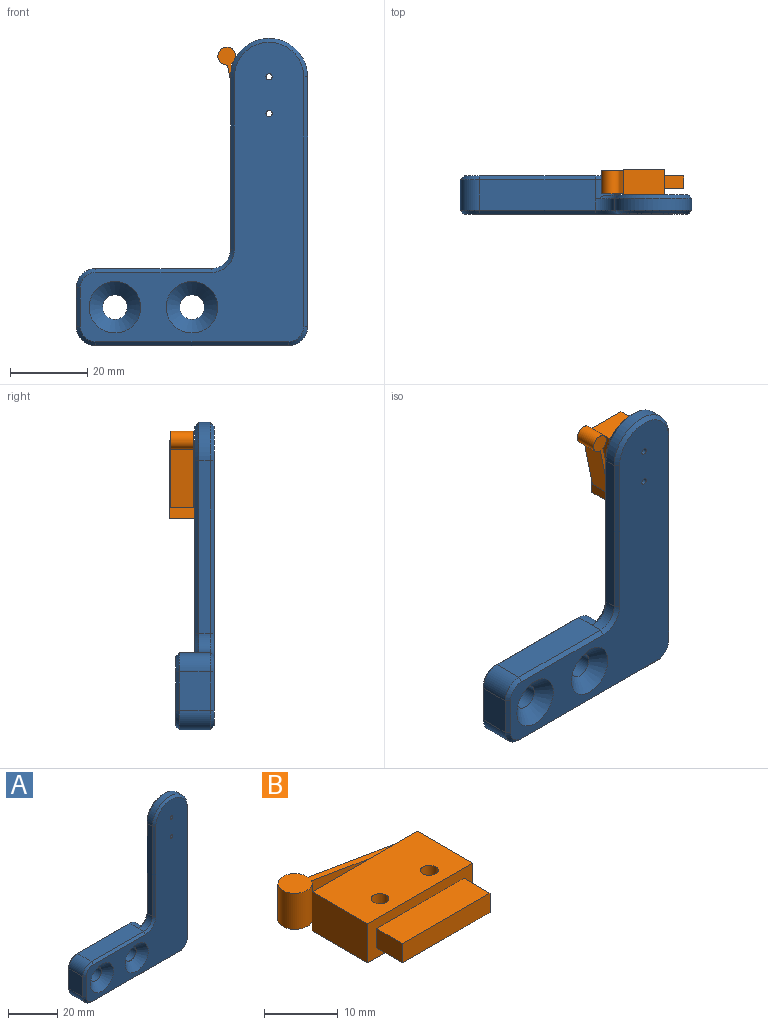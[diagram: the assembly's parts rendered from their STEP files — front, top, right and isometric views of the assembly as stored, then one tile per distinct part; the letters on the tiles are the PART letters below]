
ASSEMBLY  parts=2 mates=1
PART A: 48 faces, bbox 60x10x79.8 mm
  f0: plane 64.75x3mm, normal (1,0,0), area 194.2mm2, adj f3,f20,f26,f45
  f1: plane 38x18mm, normal (0,1,0), area 559.4mm2, adj f32,f33,f34,f35,f36,f37,f38,f39
  f2: plane 50x8mm, normal (0,0,-1), area 300mm2, adj f17,f19,f20,f30,f34,f47
  f3: cylinder r=10mm len=20mm, axis (0,1,0), area 94.2mm2, adj f0,f4,f24,f44
  f4: plane 44.75x3mm, normal (-1,0,0), area 134.2mm2, adj f3,f21,f22,f43
  f5: plane 30x8mm, normal (0,0,1), area 240mm2, adj f16,f18,f21,f25,f37
  f6: cylinder r=3.2mm len=6.4mm, axis (0,1,0), area 110.6mm2, adj f13,f41
  f7: cylinder r=0.8mm len=5mm, axis (0,1,0), area 25.1mm2, adj f11,f14
  f8: cylinder r=0.8mm len=5mm, axis (0,1,0), area 25.1mm2, adj f11,f14
  f9: plane 10x8mm, normal (-1,0,0), area 80mm2, adj f18,f19,f29,f33
  f10: cylinder r=3.2mm len=6.4mm, axis (0,1,0), area 110.6mm2, adj f12,f40
  f11: plane 77.75x58mm, normal (0,-1,0), area 1796.1mm2, adj f7,f8,f12,f13,f22,f23,f24,f25
  f12: cone r=3.2mm half-angle=45deg, axis (0,-1,0), area 153.9mm2, adj f10,f11
  f13: cone r=3.2mm half-angle=45deg, axis (0,-1,0), area 153.9mm2, adj f6,f11
  f14: plane 77.75x21.72mm, normal (0,1,0), area 1387.3mm2, adj f7,f8,f15,f16,f17,f42,f43,f44
  f15: plane 10x4mm, normal (1,0,0), area 40mm2, adj f14,f16,f17,f38
  f16: cylinder r=5mm len=5mm, axis (0,-1,0), area 33mm2, adj f5,f14,f15,f39,f42
  f17: cylinder r=5mm len=5mm, axis (0,-1,0), area 33.5mm2, adj f2,f14,f15,f36,f47
  f18: cylinder r=5mm len=8mm, axis (0,1,0), area 62.8mm2, adj f5,f9,f27,f35
  f19: cylinder r=5mm len=8mm, axis (0,1,0), area 62.8mm2, adj f2,f9,f31,f32
  f20: cylinder r=5mm len=5mm, axis (0,1,0), area 23.6mm2, adj f0,f2,f28,f46
  f21: cylinder r=5mm len=5mm, axis (0,-1,0), area 23.6mm2, adj f4,f5,f23,f42
  f22: plane 44.75x1mm, normal (-0.71,-0.71,0), area 63.3mm2, adj f4,f11,f23,f24
  f23: cone r=6mm half-angle=45deg, axis (0,-1,0), area 12.2mm2, adj f11,f21,f22,f25
  f24: cone r=9mm half-angle=45deg, axis (0,1,0), area 42.2mm2, adj f3,f11,f22,f26
  f25: plane 30x1mm, normal (0,-0.71,0.71), area 42.4mm2, adj f5,f11,f23,f27
  f26: plane 64.75x1mm, normal (0.71,-0.71,0), area 91.6mm2, adj f0,f11,f24,f28
  f27: cone r=4mm half-angle=45deg, axis (0,1,0), area 10mm2, adj f11,f18,f25,f29
  f28: cone r=4mm half-angle=45deg, axis (0,1,0), area 10mm2, adj f11,f20,f26,f30
  f29: plane 10x1mm, normal (-0.71,-0.71,0), area 14.1mm2, adj f9,f11,f27,f31
  f30: plane 50x1mm, normal (0,-0.71,-0.71), area 70.7mm2, adj f2,f11,f28,f31
  f31: cone r=4mm half-angle=45deg, axis (0,1,0), area 10mm2, adj f11,f19,f29,f30
  f32: cone r=4mm half-angle=45deg, axis (0,-1,0), area 10mm2, adj f1,f19,f33,f34
  f33: plane 10x1mm, normal (-0.71,0.71,0), area 14.1mm2, adj f1,f9,f32,f35
  f34: plane 30x1mm, normal (0,0.71,-0.71), area 42.4mm2, adj f1,f2,f32,f36
  f35: cone r=4mm half-angle=45deg, axis (0,-1,0), area 10mm2, adj f1,f18,f33,f37
  f36: cone r=4mm half-angle=45deg, axis (0,-1,0), area 10mm2, adj f1,f17,f34,f38
  f37: plane 30x1mm, normal (0,0.71,0.71), area 42.4mm2, adj f1,f5,f35,f39
  f38: plane 10x1mm, normal (0.71,0.71,0), area 14.1mm2, adj f1,f15,f36,f39
  f39: cone r=4mm half-angle=45deg, axis (0,-1,0), area 10mm2, adj f1,f16,f37,f38
  f40: cone r=4.2mm half-angle=45deg, axis (0,1,0), area 32.9mm2, adj f1,f10
  f41: cone r=4.2mm half-angle=45deg, axis (0,1,0), area 32.9mm2, adj f1,f6
  f42: cone r=6mm half-angle=45deg, axis (0,1,0), area 10mm2, adj f14,f16,f21,f43
  f43: plane 44.75x1mm, normal (-0.71,0.71,0), area 63.3mm2, adj f4,f14,f42,f44
  f44: cone r=10mm half-angle=45deg, axis (0,-1,0), area 42.2mm2, adj f3,f14,f43,f45
  f45: plane 64.75x1mm, normal (0.71,0.71,0), area 91.6mm2, adj f0,f14,f44,f46
  f46: cone r=4mm half-angle=45deg, axis (0,-1,0), area 10mm2, adj f14,f20,f45,f47
  f47: plane 20x1mm, normal (0,0.71,-0.71), area 25.4mm2, adj f2,f14,f17,f46
PART B: 18 faces, bbox 22.6x21.3x6.5 mm
  f0: plane 20.25x6.5mm, normal (0,-1,0), area 77.9mm2, adj f1,f5,f6,f7,f8,f9,f11,f12
  f1: plane 10.7x6.5mm, normal (1,0,0), area 69.5mm2, adj f0,f2,f6,f7
  f2: plane 20.25x6.5mm, normal (0,1,0), area 101.6mm2, adj f1,f5,f6,f7,f14,f15,f16,f17
  f3: cylinder r=1.2mm len=6.5mm, axis (0,0,-1), area 49mm2, adj f6,f7
  f4: cylinder r=1.2mm len=6.5mm, axis (0,0,-1), area 49mm2, adj f6,f7
  f5: plane 10.7x6.5mm, normal (-1,0,0), area 69.5mm2, adj f0,f2,f6,f7
  f6: plane 20.25x10.7mm, normal (0,0,1), area 207.6mm2, adj f0,f1,f2,f3,f4,f5
  f7: plane 20.25x10.7mm, normal (0,0,-1), area 207.6mm2, adj f0,f1,f2,f3,f4,f5
  f8: plane 5x3.2mm, normal (1,0,0), area 16mm2, adj f0,f10,f11,f12
  f9: plane 5x3.2mm, normal (-1,0,0), area 16mm2, adj f0,f10,f11,f12
  f10: plane 16.8x3.2mm, normal (0,-1,0), area 53.8mm2, adj f8,f9,f11,f12
  f11: plane 16.8x5mm, normal (0,0,1), area 84mm2, adj f0,f8,f9,f10
  f12: plane 16.8x5mm, normal (0,0,-1), area 84mm2, adj f0,f8,f9,f10
  f13: cylinder r=2.32mm len=6mm, axis (0,0,-1), area 81.6mm2, adj f14,f15,f16,f17
  f14: plane 10.51x6mm, normal (-0.2,-0.98,0), area 64.3mm2, adj f2,f13,f16,f17
  f15: plane 15.22x6mm, normal (0.2,0.98,0), area 93.2mm2, adj f2,f13,f16,f17
  f16: plane 19.87x5.6mm, normal (0,0,1), area 30.1mm2, adj f2,f13,f14,f15
  f17: plane 19.87x5.6mm, normal (0,0,-1), area 30.1mm2, adj f2,f13,f14,f15
PLACE A t=(0,-6.5,-5)mm
PLACE B rot(axis=(-0.58,0.58,0.58),120deg) t=(-2.35,-8.25,50)mm fixed
MATE fastened A.f8 <-> B.f3  axis (0,1,0) through (0,-11.5,54.75)mm
